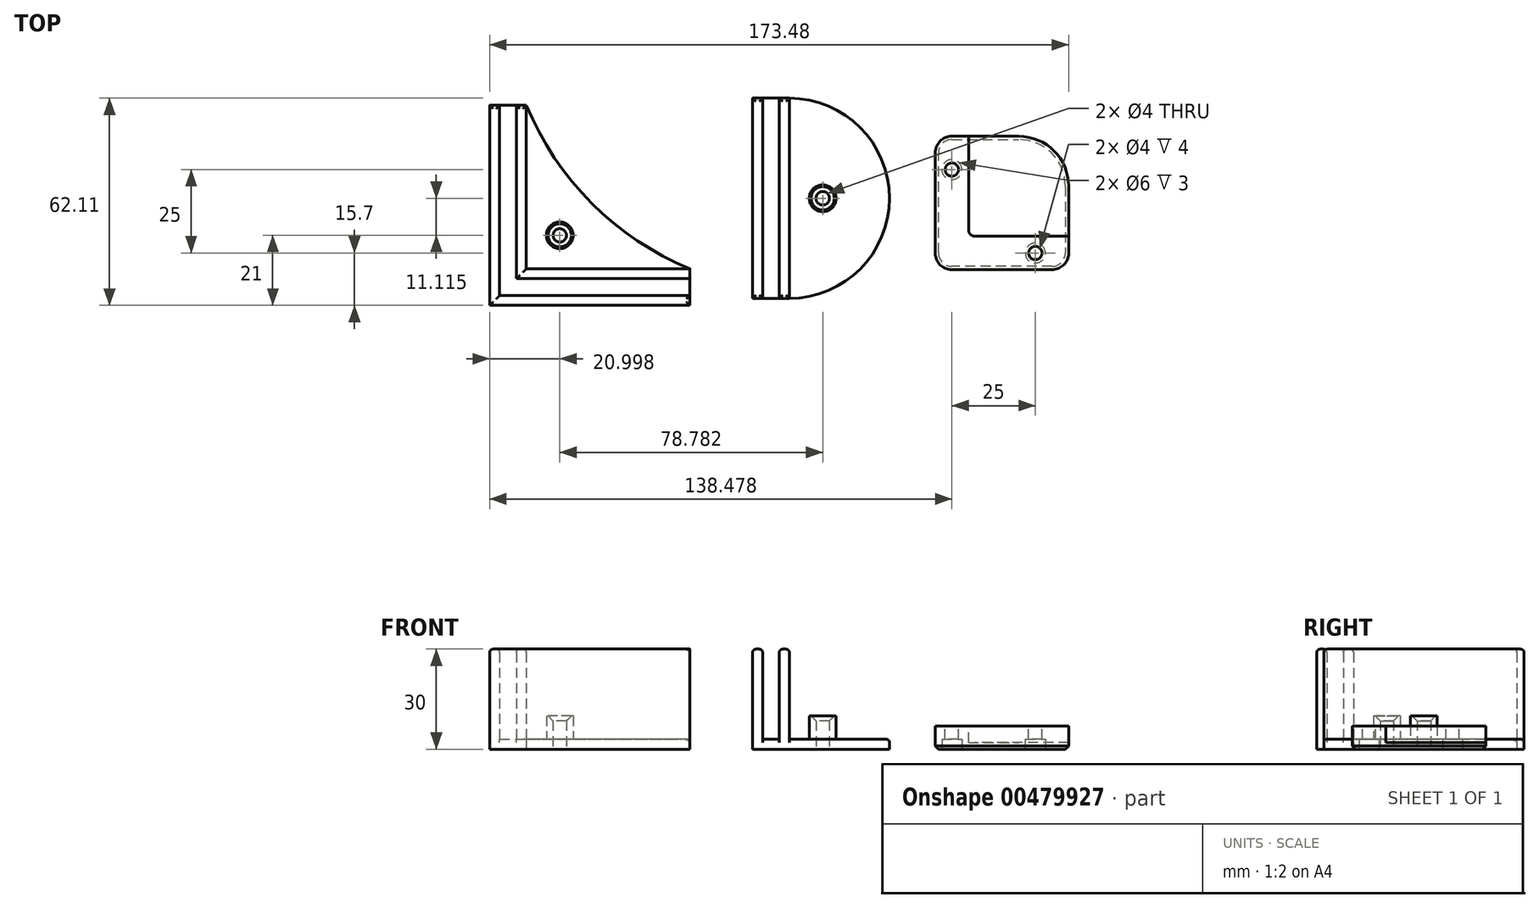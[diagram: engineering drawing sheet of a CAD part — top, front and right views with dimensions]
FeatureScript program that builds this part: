
annotation { "Feature Type Name" : "Feature", "Feature Type Description" : "" }
export const myFeature = defineFeature(function(context is Context, id is Id, definition is map)
    precondition{}
    {
        {
            var Q0;
            Q0=qCreatedBy(makeId("Top.planeOp"),FACE);
            var sketch = newSketch(context, id + "F0", { "sketchPlane" : qUnion([Q0])});
            skLineSegment(sketch, "E0.bottom", {"start": v(-78.78, 29.3) * mm, "end": v(-67.78, 29.3) * mm});
            skLineSegment(sketch, "E0.top", {"start": v(-78.78, -30.7) * mm, "end": v(-18.78, -30.7) * mm});
            skLineSegment(sketch, "E0.left", {"start": v(-78.78, 29.3) * mm, "end": v(-78.78, -30.7) * mm});
            skLineSegment(sketch, "E0.right", {"start": v(-18.78, -19.7) * mm, "end": v(-18.78, -30.7) * mm});
            skLineSegment(sketch, "E1.top", {"start": v(-18.78, -19.7) * mm, "end": v(-67.78, -19.7) * mm});
            skLineSegment(sketch, "E1.right", {"start": v(-67.78, 29.3) * mm, "end": v(-67.78, -19.7) * mm});
            skArc(sketch, "E2", {"start": v(-67.78, 29.3) * mm, "mid": v(-48.19, -0.1) * mm, "end": v(-18.78, -19.7) * mm});
            skCircle(sketch, "E3", {"center": v(-57.78, -9.7) * mm, "radius": 2 * mm});
            skCircle(sketch, "E4", {"center": v(-57.78, -9.7) * mm, "radius": 4 * mm});
            skLineSegment(sketch, "E5.0", {"start": v(-75.78, -27.7) * mm, "end": v(-18.78, -27.7) * mm});
            skLineSegment(sketch, "E5.1", {"start": v(-75.78, 29.3) * mm, "end": v(-75.78, -27.7) * mm});
            skLineSegment(sketch, "E6.0", {"start": v(-18.78, -22.7) * mm, "end": v(-70.78, -22.7) * mm});
            skLineSegment(sketch, "E6.1", {"start": v(-70.78, 29.3) * mm, "end": v(-70.78, -22.7) * mm});
            skSolve(sketch);
        }
        {
            var Q0;
            Q0=makeQuery(id+"F0.imprint","IMPRINT",FACE,{"disambiguationData":[TD([[makeQuery(id+"F0.imprint","IMPRINT",EDGE,{"derivedFrom":sQuery(id+"F0.wireOp",EDGE,"E1.top")}),-1.0]])]});
            var Q1;
            {var subQ1=sQuery(id+"F0.wireOp",EDGE,"E5.0");Q1=makeQuery(id+"F0.imprint","IMPRINT",FACE,{"disambiguationData":[TD([[makeQuery(id+"F0.imprint","IMPRINT",EDGE,{"derivedFrom":subQ1}),1.0]])]});}
            extrude(context, id + "F1", {"entities" : qUnion([Q0, Q1]), "depth" : 3 * mm});
        }
        {
            var Q0;
            {var subQ1=sQuery(id+"F0.wireOp",EDGE,"E0.top");Q0=makeQuery(id+"F0.imprint","IMPRINT",FACE,{"disambiguationData":[TD([[makeQuery(id+"F0.imprint","IMPRINT",EDGE,{"derivedFrom":subQ1}),1.0]])]});}
            var Q1;
            {var subQ1=sQuery(id+"F0.wireOp",EDGE,"E1.top");Q1=makeQuery(id+"F0.imprint","IMPRINT",FACE,{"disambiguationData":[TD([[makeQuery(id+"F0.imprint","IMPRINT",EDGE,{"derivedFrom":subQ1}),1.0]])]});}
            extrude(context, id + "F2", {"entities" : qUnion([Q0, Q1]), "operationType" : NewBodyOperationType.ADD, "depth" : 30 * mm});
        }
        {
            var Q0;
            Q0=makeQuery(id+"F0.imprint","IMPRINT",FACE,{"disambiguationData":[TD([[makeQuery(id+"F0.imprint","IMPRINT",EDGE,{"derivedFrom":sQuery(id+"F0.wireOp",EDGE,"E3")}),-1.0]])]});
            extrude(context, id + "F3", {"entities" : qUnion([Q0]), "operationType" : NewBodyOperationType.ADD, "depth" : 10 * mm});
        }
        {
            var Q0;
            Q0=makeQuery(id+"F2.opExtrude","CAP_EDGE",EDGE,{"disambiguationData":[OSD([sQuery(id+"F0.wireOp",EDGE,"E0.left")])],"isStart":false});
            var Q1;
            Q1=makeQuery(id+"F2.opExtrude","CAP_EDGE",EDGE,{"disambiguationData":[OSD([sQuery(id+"F0.wireOp",EDGE,"E0.top")])],"isStart":false});
            var Q2;
            Q2=makeQuery(id+"F2.opExtrude","CAP_EDGE",EDGE,{"disambiguationData":[OSD([sQuery(id+"F0.wireOp",EDGE,"E6.0")])],"isStart":false});
            var Q3;
            Q3=makeQuery(id+"F2.opExtrude","CAP_EDGE",EDGE,{"disambiguationData":[OSD([sQuery(id+"F0.wireOp",EDGE,"E6.1")])],"isStart":false});
            var Q4;
            Q4=makeQuery(id+"F2.opExtrude","CAP_EDGE",EDGE,{"disambiguationData":[OSD([sQuery(id+"F0.wireOp",EDGE,"E1.right")])],"isStart":false});
            var Q5;
            Q5=makeQuery(id+"F2.opExtrude","CAP_EDGE",EDGE,{"disambiguationData":[OSD([sQuery(id+"F0.wireOp",EDGE,"E1.top")])],"isStart":false});
            var Q6;
            Q6=makeQuery(id+"F2.opExtrude","CAP_EDGE",EDGE,{"disambiguationData":[OSD([sQuery(id+"F0.wireOp",EDGE,"E5.1")])],"isStart":false});
            var Q7;
            Q7=makeQuery(id+"F2.opExtrude","CAP_EDGE",EDGE,{"disambiguationData":[OSD([sQuery(id+"F0.wireOp",EDGE,"E5.0")])],"isStart":false});
            var Q8;
            {var subQ0=sQuery(id+"F0.wireOp",EDGE,"E0.bottom");Q8=makeQuery(id+"F2.opExtrude","CAP_EDGE",EDGE,{"disambiguationData":[OSD([subQ0]),TDD([makeQuery(id+"F0.imprint","IMPRINT",EDGE,{"disambiguationData":[TD([[makeQuery(id+"F0.imprint","INTERSECT",VERTEX,{"derivedFrom":[subQ0,sQuery(id+"F0.wireOp",EDGE,"E0.left")]}),-1.0]])],"derivedFrom":subQ0})])],"isStart":false});}
            var Q9;
            {var subQ0=sQuery(id+"F0.wireOp",EDGE,"E0.bottom");Q9=makeQuery(id+"F2.opExtrude","CAP_EDGE",EDGE,{"disambiguationData":[OSD([subQ0]),TDD([makeQuery(id+"F0.imprint","IMPRINT",EDGE,{"disambiguationData":[TD([[makeQuery(id+"F0.imprint","INTERSECT",VERTEX,{"derivedFrom":[subQ0,sQuery(id+"F0.wireOp",EDGE,"E6.1")]}),-1.0]])],"derivedFrom":subQ0})])],"isStart":false});}
            var Q10;
            {var subQ0=sQuery(id+"F0.wireOp",EDGE,"E0.right");Q10=makeQuery(id+"F2.opExtrude","CAP_EDGE",EDGE,{"disambiguationData":[OSD([subQ0]),TDD([makeQuery(id+"F0.imprint","IMPRINT",EDGE,{"disambiguationData":[TD([[makeQuery(id+"F0.imprint","INTERSECT",VERTEX,{"derivedFrom":[sQuery(id+"F0.wireOp",EDGE,"E0.top"),subQ0]}),1.0]])],"derivedFrom":subQ0})])],"isStart":false});}
            var Q11;
            Q11=makeQuery(id+"F1.opExtrude","CAP_EDGE",EDGE,{"disambiguationData":[OSD([sQuery(id+"F0.wireOp",EDGE,"E2")])],"isStart":false});
            var Q12;
            Q12=makeQuery(id+"F1.opExtrude","CAP_EDGE",EDGE,{"disambiguationData":[OSD([sQuery(id+"F0.wireOp",EDGE,"E0.right")])],"isStart":false});
            var Q13;
            Q13=makeQuery(id+"F1.opExtrude","CAP_EDGE",EDGE,{"disambiguationData":[OSD([sQuery(id+"F0.wireOp",EDGE,"E0.bottom")])],"isStart":false});
            fillet(context, id + "F4", {"entities" : qUnion([Q0, Q1, Q2, Q3, Q4, Q5, Q6, Q7, Q8, Q9, Q10, Q11, Q12, Q13]), "radius" : 1 * mm, "tangentPropagation" : true, "allowEdgeOverflow" : false});
        }
        {
            var Q0;
            Q0=makeQuery(id+"F3.opExtrude","CAP_EDGE",EDGE,{"disambiguationData":[OSD([sQuery(id+"F0.wireOp",EDGE,"E3")])],"isStart":false});
            chamfer(context, id + "F5", {"entities" : qUnion([Q0]), "width" : 1.5 * mm, "tangentPropagation" : true});
        }
        {
            var Q0;
            Q0=qCreatedBy(makeId("Top.planeOp"),FACE);
            var sketch = newSketch(context, id + "F6", { "sketchPlane" : qUnion([Q0])});
            skLineSegment(sketch, "E7.bottom", {"start": v(0, 31.41) * mm, "end": v(11, 31.41) * mm});
            skLineSegment(sketch, "E7.top", {"start": v(0, -28.59) * mm, "end": v(11, -28.59) * mm});
            skLineSegment(sketch, "E7.left", {"start": v(0, 31.41) * mm, "end": v(0, -28.59) * mm});
            skLineSegment(sketch, "E7.right", {"start": v(11, 31.41) * mm, "end": v(11, -28.59) * mm});
            skLineSegment(sketch, "E8.0", {"start": v(3, 31.41) * mm, "end": v(3, -28.59) * mm});
            skLineSegment(sketch, "E9.0", {"start": v(8, 31.41) * mm, "end": v(8, -28.59) * mm});
            skArc(sketch, "E10", {"start": v(11, -28.59) * mm, "mid": v(41, 1.41) * mm, "end": v(11, 31.41) * mm});
            skCircle(sketch, "E11", {"center": v(21, 1.41) * mm, "radius": 2 * mm});
            skCircle(sketch, "E12", {"center": v(21, 1.41) * mm, "radius": 4 * mm});
            skSolve(sketch);
        }
        {
            var Q0;
            {var subQ0=sQuery(id+"F6.wireOp",EDGE,"E8.0");Q0=makeQuery(id+"F6.imprint","IMPRINT",FACE,{"disambiguationData":[TD([[makeQuery(id+"F6.imprint","IMPRINT",EDGE,{"derivedFrom":subQ0}),1.0]])]});}
            var Q1;
            Q1=makeQuery(id+"F6.imprint","IMPRINT",FACE,{"disambiguationData":[TD([[makeQuery(id+"F6.imprint","IMPRINT",EDGE,{"derivedFrom":sQuery(id+"F6.wireOp",EDGE,"E7.right")}),1.0]])]});
            extrude(context, id + "F7", {"entities" : qUnion([Q0, Q1]), "depth" : 3 * mm});
        }
        {
            var Q0;
            {var subQ0=sQuery(id+"F6.wireOp",EDGE,"E7.left");Q0=makeQuery(id+"F6.imprint","IMPRINT",FACE,{"disambiguationData":[TD([[makeQuery(id+"F6.imprint","IMPRINT",EDGE,{"derivedFrom":subQ0}),1.0]])]});}
            var Q1;
            {var subQ1=sQuery(id+"F6.wireOp",EDGE,"E7.right");Q1=makeQuery(id+"F6.imprint","IMPRINT",FACE,{"disambiguationData":[TD([[makeQuery(id+"F6.imprint","IMPRINT",EDGE,{"derivedFrom":subQ1}),-1.0]])]});}
            extrude(context, id + "F8", {"entities" : qUnion([Q0, Q1]), "operationType" : NewBodyOperationType.ADD, "depth" : 30 * mm});
        }
        {
            var Q0;
            Q0=makeQuery(id+"F6.imprint","IMPRINT",FACE,{"disambiguationData":[TD([[makeQuery(id+"F6.imprint","IMPRINT",EDGE,{"derivedFrom":sQuery(id+"F6.wireOp",EDGE,"E11")}),-1.0]])]});
            extrude(context, id + "F9", {"entities" : qUnion([Q0]), "operationType" : NewBodyOperationType.ADD, "depth" : 10 * mm});
        }
        {
            var Q0;
            Q0=makeQuery(id+"F9.opExtrude","CAP_EDGE",EDGE,{"disambiguationData":[OSD([sQuery(id+"F6.wireOp",EDGE,"E11")])],"isStart":false});
            chamfer(context, id + "F10", {"entities" : qUnion([Q0]), "width" : 1.5 * mm, "tangentPropagation" : true});
        }
        {
            var Q0;
            Q0=makeQuery(id+"F8.opExtrude","CAP_EDGE",EDGE,{"disambiguationData":[OSD([sQuery(id+"F6.wireOp",EDGE,"E7.left")])],"isStart":false});
            var Q1;
            Q1=makeQuery(id+"F8.opExtrude","CAP_EDGE",EDGE,{"disambiguationData":[OSD([sQuery(id+"F6.wireOp",EDGE,"E8.0")])],"isStart":false});
            var Q2;
            Q2=makeQuery(id+"F8.opExtrude","CAP_EDGE",EDGE,{"disambiguationData":[OSD([sQuery(id+"F6.wireOp",EDGE,"E9.0")])],"isStart":false});
            var Q3;
            Q3=makeQuery(id+"F8.opExtrude","CAP_EDGE",EDGE,{"disambiguationData":[OSD([sQuery(id+"F6.wireOp",EDGE,"E7.right")])],"isStart":false});
            var Q4;
            {var subQ0=sQuery(id+"F6.wireOp",EDGE,"E7.top");Q4=makeQuery(id+"F8.opExtrude","CAP_EDGE",EDGE,{"disambiguationData":[OSD([subQ0]),TDD([makeQuery(id+"F6.imprint","IMPRINT",EDGE,{"disambiguationData":[TD([[makeQuery(id+"F6.imprint","INTERSECT",VERTEX,{"derivedFrom":[subQ0,sQuery(id+"F6.wireOp",EDGE,"E9.0")]}),-1.0]])],"derivedFrom":subQ0})])],"isStart":false});}
            var Q5;
            {var subQ0=sQuery(id+"F6.wireOp",EDGE,"E7.top");Q5=makeQuery(id+"F8.opExtrude","CAP_EDGE",EDGE,{"disambiguationData":[OSD([subQ0]),TDD([makeQuery(id+"F6.imprint","IMPRINT",EDGE,{"disambiguationData":[TD([[makeQuery(id+"F6.imprint","INTERSECT",VERTEX,{"derivedFrom":[subQ0,sQuery(id+"F6.wireOp",EDGE,"E7.left")]}),-1.0]])],"derivedFrom":subQ0})])],"isStart":false});}
            var Q6;
            Q6=makeQuery(id+"F7.opExtrude","CAP_EDGE",EDGE,{"disambiguationData":[OSD([sQuery(id+"F6.wireOp",EDGE,"E7.top")])],"isStart":false});
            var Q7;
            Q7=makeQuery(id+"F7.opExtrude","CAP_EDGE",EDGE,{"disambiguationData":[OSD([sQuery(id+"F6.wireOp",EDGE,"E10")])],"isStart":false});
            var Q8;
            {var subQ0=sQuery(id+"F6.wireOp",EDGE,"E7.bottom");Q8=makeQuery(id+"F8.opExtrude","CAP_EDGE",EDGE,{"disambiguationData":[OSD([subQ0]),TDD([makeQuery(id+"F6.imprint","IMPRINT",EDGE,{"disambiguationData":[TD([[makeQuery(id+"F6.imprint","INTERSECT",VERTEX,{"derivedFrom":[subQ0,sQuery(id+"F6.wireOp",EDGE,"E7.left")]}),-1.0]])],"derivedFrom":subQ0})])],"isStart":false});}
            var Q9;
            {var subQ0=sQuery(id+"F6.wireOp",EDGE,"E7.bottom");Q9=makeQuery(id+"F8.opExtrude","CAP_EDGE",EDGE,{"disambiguationData":[OSD([subQ0]),TDD([makeQuery(id+"F6.imprint","IMPRINT",EDGE,{"disambiguationData":[TD([[makeQuery(id+"F6.imprint","INTERSECT",VERTEX,{"derivedFrom":[subQ0,sQuery(id+"F6.wireOp",EDGE,"E9.0")]}),-1.0]])],"derivedFrom":subQ0})])],"isStart":false});}
            var Q10;
            Q10=makeQuery(id+"F7.opExtrude","CAP_EDGE",EDGE,{"disambiguationData":[OSD([sQuery(id+"F6.wireOp",EDGE,"E7.bottom")])],"isStart":false});
            fillet(context, id + "F11", {"entities" : qUnion([Q0, Q1, Q2, Q3, Q4, Q5, Q6, Q7, Q8, Q9, Q10]), "radius" : 1 * mm, "tangentPropagation" : true, "allowEdgeOverflow" : false});
        }
        {
            var Q0;
            Q0=qCreatedBy(makeId("Top.planeOp"),FACE);
            var sketch = newSketch(context, id + "F12", { "sketchPlane" : qUnion([Q0])});
            skLineSegment(sketch, "E13.bottom", {"start": v(54.7, 20) * mm, "end": v(94.7, 20) * mm});
            skLineSegment(sketch, "E13.top", {"start": v(54.7, -20) * mm, "end": v(94.7, -20) * mm});
            skLineSegment(sketch, "E13.left", {"start": v(54.7, 20) * mm, "end": v(54.7, -20) * mm});
            skLineSegment(sketch, "E13.right", {"start": v(94.7, 20) * mm, "end": v(94.7, -20) * mm});
            skSolve(sketch);
        }
        {
            var Q0;
            Q0=makeQuery(id+"F12.imprint","IMPRINT",FACE,{"disambiguationData":[TD([[makeQuery(id+"F12.imprint","IMPRINT",EDGE,{"derivedFrom":sQuery(id+"F12.wireOp",EDGE,"E13.bottom")}),-1.0]])]});
            extrude(context, id + "F13", {"entities" : qUnion([Q0]), "depth" : 7 * mm, "offsetDistance" : 25 * mm});
        }
        {
            var Q0;
            Q0=makeQuery(id+"F13.opExtrude","CAP_FACE",FACE,{"disambiguationData":[OSD([sQuery(id+"F12.wireOp",EDGE,"E13.bottom"),sQuery(id+"F12.wireOp",EDGE,"E13.top"),sQuery(id+"F12.wireOp",EDGE,"E13.left"),sQuery(id+"F12.wireOp",EDGE,"E13.right")])],"isStart":false});
            var sketch = newSketch(context, id + "F14", { "sketchPlane" : qUnion([Q0])});
            skLineSegment(sketch, "E14.bottom", {"start": v(94.7, 20) * mm, "end": v(64.7, 20) * mm});
            skLineSegment(sketch, "E14.top", {"start": v(94.7, -10) * mm, "end": v(64.7, -10) * mm});
            skLineSegment(sketch, "E14.left", {"start": v(94.7, 20) * mm, "end": v(94.7, -10) * mm});
            skLineSegment(sketch, "E14.right", {"start": v(64.7, 20) * mm, "end": v(64.7, -10) * mm});
            skCircle(sketch, "E15", {"center": v(59.7, 10) * mm, "radius": 2 * mm});
            skCircle(sketch, "E16", {"center": v(84.7, -15) * mm, "radius": 2 * mm});
            skSolve(sketch);
        }
        {
            var Q0;
            Q0=makeQuery(id+"F14.imprint","IMPRINT",FACE,{"disambiguationData":[TD([[makeQuery(id+"F14.imprint","IMPRINT",EDGE,{"derivedFrom":sQuery(id+"F14.wireOp",EDGE,"E14.bottom")}),-1.0]])]});
            extrude(context, id + "F15", {"entities" : qUnion([Q0]), "operationType" : NewBodyOperationType.REMOVE, "oppositeDirection" : true, "depth" : 5 * mm, "offsetDistance" : 25 * mm});
        }
        {
            var Q0;
            Q0=makeQuery(id+"F14.imprint","IMPRINT",FACE,{"disambiguationData":[TD([[makeQuery(id+"F14.imprint","IMPRINT",EDGE,{"derivedFrom":sQuery(id+"F14.wireOp",EDGE,"E15")}),1.0]])]});
            var Q1;
            Q1=makeQuery(id+"F14.imprint","IMPRINT",FACE,{"disambiguationData":[TD([[makeQuery(id+"F14.imprint","IMPRINT",EDGE,{"derivedFrom":sQuery(id+"F14.wireOp",EDGE,"E16")}),1.0]])]});
            extrude(context, id + "F16", {"entities" : qUnion([Q0, Q1]), "operationType" : NewBodyOperationType.REMOVE, "oppositeDirection" : true, "depth" : 25 * mm, "offsetDistance" : 25 * mm});
        }
        {
            var Q0;
            Q0=makeQuery(id+"F13.opExtrude","CAP_FACE",FACE,{"disambiguationData":[OSD([sQuery(id+"F12.wireOp",EDGE,"E13.bottom"),sQuery(id+"F12.wireOp",EDGE,"E13.top"),sQuery(id+"F12.wireOp",EDGE,"E13.left"),sQuery(id+"F12.wireOp",EDGE,"E13.right")])],"isStart":true});
            var sketch = newSketch(context, id + "F17", { "sketchPlane" : qUnion([Q0])});
            skCircle(sketch, "E17", {"center": v(59.7, -10) * mm, "radius": 3 * mm});
            skCircle(sketch, "E18", {"center": v(84.7, 15) * mm, "radius": 3 * mm});
            skSolve(sketch);
        }
        {
            var Q0;
            Q0=makeQuery(id+"F17.imprint","IMPRINT",FACE,{"disambiguationData":[TD([[makeQuery(id+"F17.imprint","IMPRINT",EDGE,{"derivedFrom":sQuery(id+"F17.wireOp",EDGE,"E17")}),1.0]])]});
            var Q1;
            Q1=makeQuery(id+"F17.imprint","IMPRINT",FACE,{"disambiguationData":[TD([[makeQuery(id+"F17.imprint","IMPRINT",EDGE,{"derivedFrom":sQuery(id+"F17.wireOp",EDGE,"E18")}),1.0]])]});
            extrude(context, id + "F18", {"entities" : qUnion([Q0, Q1]), "operationType" : NewBodyOperationType.REMOVE, "oppositeDirection" : true, "depth" : 3 * mm, "offsetDistance" : 25 * mm});
        }
        {
            var Q0;
            Q0=makeQuery(id+"F13.opExtrude","SWEPT_EDGE",EDGE,{"disambiguationData":[OSD([sQuery(id+"F12.wireOp",EDGE,"E13.bottom"),sQuery(id+"F12.wireOp",EDGE,"E13.right")])]});
            fillet(context, id + "F19", {"entities" : qUnion([Q0]), "radius" : 15 * mm, "tangentPropagation" : true, "allowEdgeOverflow" : false});
        }
        {
            var Q0;
            Q0=makeQuery(id+"F13.opExtrude","SWEPT_EDGE",EDGE,{"disambiguationData":[OSD([sQuery(id+"F12.wireOp",EDGE,"E13.bottom"),sQuery(id+"F12.wireOp",EDGE,"E13.left")])]});
            var Q1;
            Q1=makeQuery(id+"F13.opExtrude","SWEPT_EDGE",EDGE,{"disambiguationData":[OSD([sQuery(id+"F12.wireOp",EDGE,"E13.top"),sQuery(id+"F12.wireOp",EDGE,"E13.right")])]});
            var Q2;
            Q2=makeQuery(id+"F13.opExtrude","SWEPT_EDGE",EDGE,{"disambiguationData":[OSD([sQuery(id+"F12.wireOp",EDGE,"E13.top"),sQuery(id+"F12.wireOp",EDGE,"E13.left")])]});
            fillet(context, id + "F20", {"entities" : qUnion([Q0, Q1, Q2]), "radius" : 5 * mm, "tangentPropagation" : true, "allowEdgeOverflow" : false});
        }
        {
            var Q0;
            Q0=makeQuery(id+"F13.opExtrude","CAP_EDGE",EDGE,{"disambiguationData":[OSD([sQuery(id+"F12.wireOp",EDGE,"E13.right")])],"isStart":true});
            var Q1;
            Q1=makeQuery(id+"F18.boolean.opBoolean","COPY",EDGE,{"derivedFrom":makeQuery(id+"F18.opExtrude","CAP_EDGE",EDGE,{"disambiguationData":[OSD([sQuery(id+"F17.wireOp",EDGE,"E17")])],"isStart":true})});
            var Q2;
            Q2=makeQuery(id+"F18.boolean.opBoolean","COPY",EDGE,{"derivedFrom":makeQuery(id+"F18.opExtrude","CAP_EDGE",EDGE,{"disambiguationData":[OSD([sQuery(id+"F17.wireOp",EDGE,"E18")])],"isStart":true})});
            chamfer(context, id + "F21", {"entities" : qUnion([Q0, Q1, Q2]), "width" : 1 * mm, "tangentPropagation" : true});
        }
        {
            var Q0;
            Q0=makeQuery(id+"F15.boolean.opBoolean","COPY",EDGE,{"derivedFrom":makeQuery(id+"F15.opExtrude","SWEPT_EDGE",EDGE,{"disambiguationData":[OSD([sQuery(id+"F12.wireOp",EDGE,"E13.bottom"),sQuery(id+"F14.wireOp",EDGE,"E14.bottom"),sQuery(id+"F14.wireOp",EDGE,"E14.right")])]})});
            var Q1;
            Q1=makeQuery(id+"F15.boolean.opBoolean","COPY",EDGE,{"derivedFrom":makeQuery(id+"F15.opExtrude","SWEPT_EDGE",EDGE,{"disambiguationData":[OSD([sQuery(id+"F12.wireOp",EDGE,"E13.right"),sQuery(id+"F14.wireOp",EDGE,"E14.top"),sQuery(id+"F14.wireOp",EDGE,"E14.left")])]})});
            var Q2;
            Q2=makeQuery(id+"F15.boolean.opBoolean","COPY",EDGE,{"derivedFrom":makeQuery(id+"F15.opExtrude","SWEPT_EDGE",EDGE,{"disambiguationData":[OSD([sQuery(id+"F14.wireOp",EDGE,"E14.top"),sQuery(id+"F14.wireOp",EDGE,"E14.right")])]})});
            fillet(context, id + "F22", {"entities" : qUnion([Q0, Q1, Q2]), "radius" : 2 * mm, "tangentPropagation" : true, "allowEdgeOverflow" : false});
        }
    });
